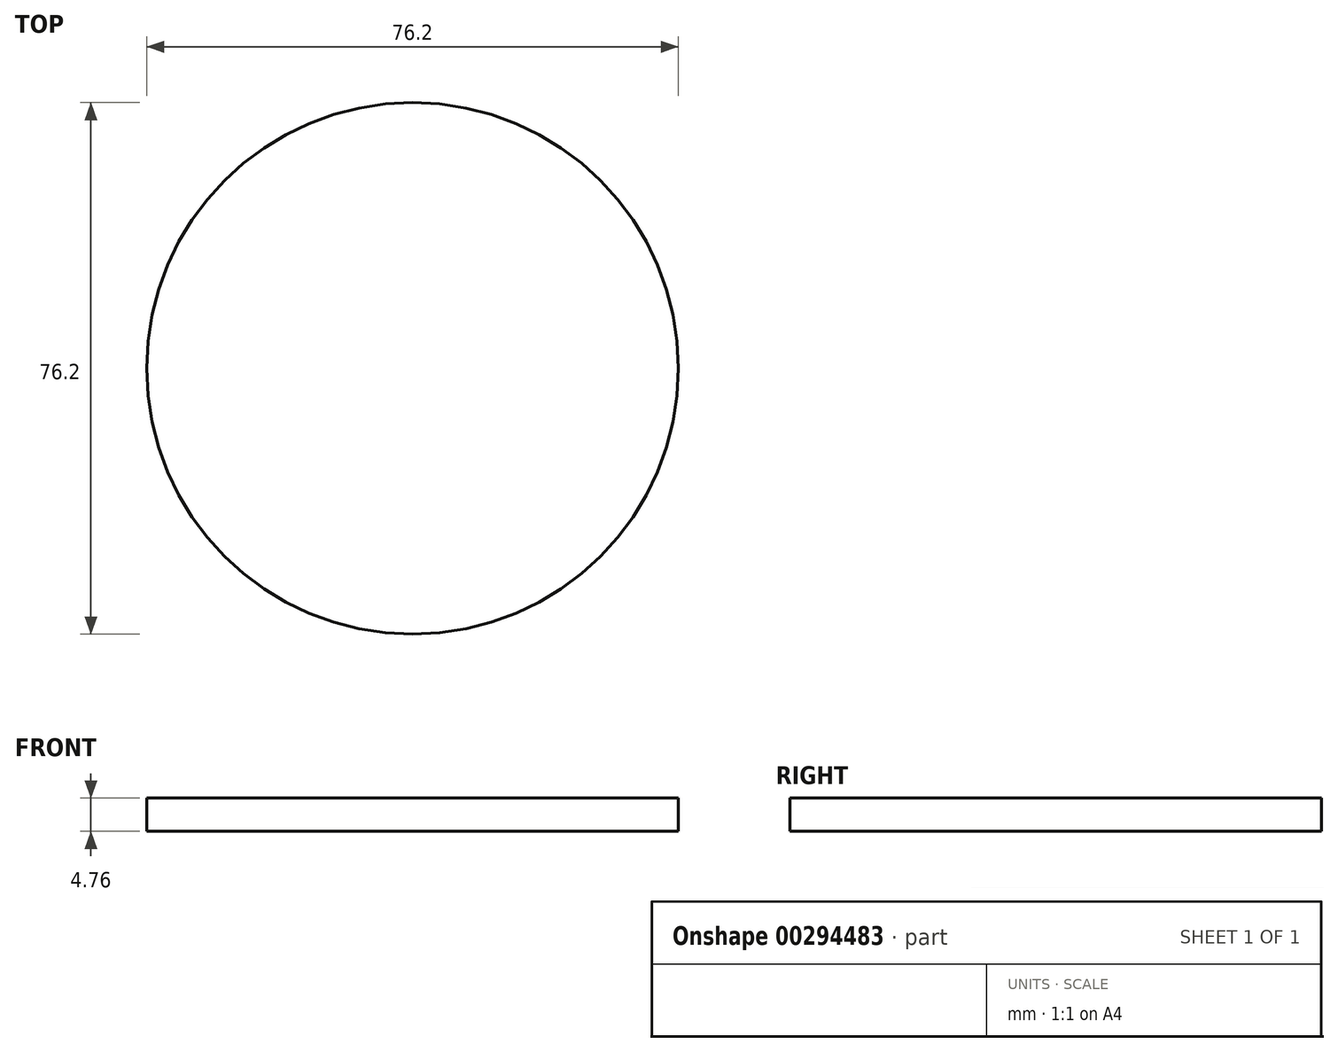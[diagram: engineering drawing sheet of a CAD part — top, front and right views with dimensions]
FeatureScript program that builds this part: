
annotation { "Feature Type Name" : "Feature", "Feature Type Description" : "" }
export const myFeature = defineFeature(function(context is Context, id is Id, definition is map)
    precondition{}
    {
        {
            var Q0;
            Q0=qCreatedBy(makeId("Top.planeOp"),FACE);
            var sketch = newSketch(context, id + "F0", { "sketchPlane" : qUnion([Q0])});
            skCircle(sketch, "E0", {"center": v(0, 0) * mm, "radius": 38.1 * mm});
            skSolve(sketch);
        }
        {
            var Q0;
            Q0 = qSketchRegion(id + "F0", true);
            extrude(context, id + "F1", {"entities" : qUnion([Q0]), "depth" : 4.76 * mm});
        }
    });
